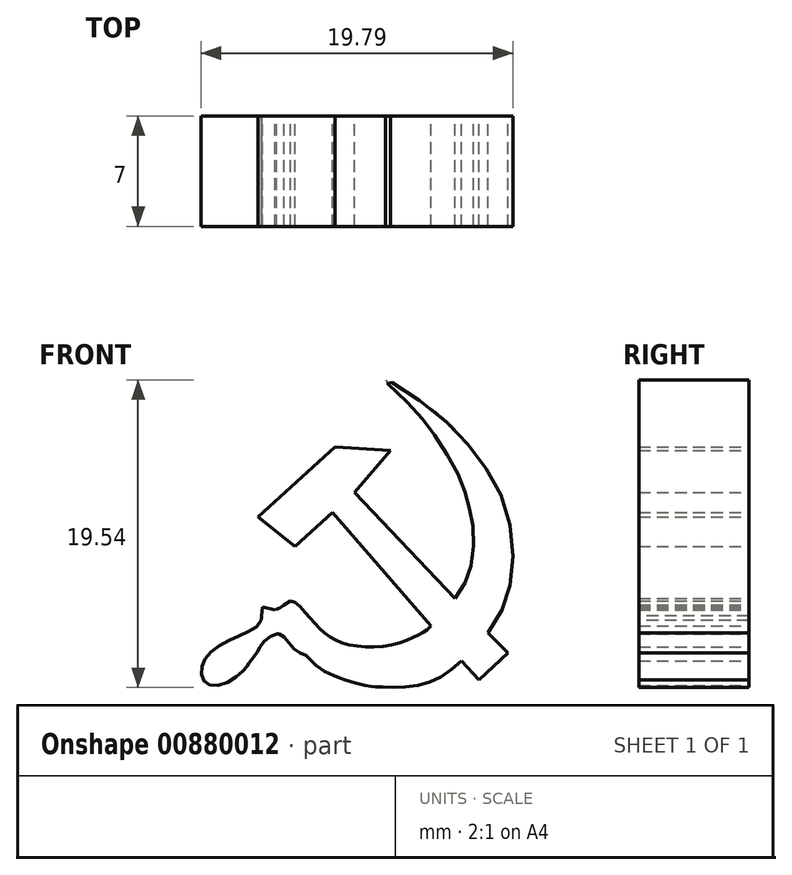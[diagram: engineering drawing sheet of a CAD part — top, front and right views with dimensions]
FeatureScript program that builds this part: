
annotation { "Feature Type Name" : "Feature", "Feature Type Description" : "" }
export const myFeature = defineFeature(function(context is Context, id is Id, definition is map)
    precondition{}
    {
        {
            var Q0;
            Q0=qCreatedBy(makeId("Front.planeOp"),FACE);
            var sketch = newSketch(context, id + "F0", { "sketchPlane" : qUnion([Q0])});
            skLineSegment(sketch, "E0", {"start": v(-4.12, 3.33) * mm, "end": v(-6.5, 1.17) * mm});
            skLineSegment(sketch, "E1", {"start": v(-6.5, 1.17) * mm, "end": v(-8.85, 3.04) * mm});
            skLineSegment(sketch, "E2", {"start": v(-8.85, 3.04) * mm, "end": v(-3.96, 7.5) * mm});
            skLineSegment(sketch, "E3", {"start": v(-3.96, 7.5) * mm, "end": v(-0.42, 7.27) * mm});
            skLineSegment(sketch, "E4", {"start": v(-0.42, 7.27) * mm, "end": v(-2.72, 4.6) * mm});
            skLineSegment(sketch, "E5", {"start": v(-2.72, 4.6) * mm, "end": v(3.66, -2.14) * mm});
            skLineSegment(sketch, "E6", {"start": v(-4.12, 3.33) * mm, "end": v(2.14, -3.89) * mm});
            skLineSegment(sketch, "E7", {"start": v(4.08, -6.1) * mm, "end": v(5.2, -7.29) * mm});
            skLineSegment(sketch, "E8", {"start": v(5.2, -7.29) * mm, "end": v(7.02, -5.6) * mm});
            skLineSegment(sketch, "E9", {"start": v(7.02, -5.6) * mm, "end": v(3.66, -2.14) * mm});
            skLineSegment(sketch, "E10", {"start": v(2.14, -3.89) * mm, "end": v(4.08, -6.1) * mm});
            skLineSegment(sketch, "E11", {"start": v(-6.78, -2.3) * mm, "end": v(-7.77, -2.87) * mm});
            skLineSegment(sketch, "E12", {"start": v(-7.77, -2.87) * mm, "end": v(-8.54, -2.68) * mm});
            skLineSegment(sketch, "E13", {"start": v(-8.54, -2.68) * mm, "end": v(-8.65, -3.54) * mm});
            skLineSegment(sketch, "E14", {"start": v(-7.96, -4.4) * mm, "end": v(-7.3, -4.4) * mm});
            skFitSpline(sketch, "E15", {"points": [v(-0.76, 11.75) * mm, v(0.78, 10.2) * mm, v(2.04, 8.7) * mm, v(3.28, 6.83) * mm, v(4.16, 5.07) * mm, v(4.57, 3.68) * mm, v(4.8, 2.47) * mm, v(4.81, 0.67) * mm, v(4.44, -0.87) * mm, v(3.66, -2.14) * mm, v(2.14, -3.89) * mm, v(1.4, -4.42) * mm, v(-0.28, -5.07) * mm, v(-2.9, -5.1) * mm, v(-4.45, -4.45) * mm, v(-5.68, -3.22) * mm, v(-6.78, -2.3) * mm, v(-7.66, -2.8) * mm, v(-8.54, -2.68) * mm, v(-8.65, -3.54) * mm, v(-9.81, -4.4) * mm, v(-11.75, -5.47) * mm, v(-12.44, -6.64) * mm, v(-12.13, -7.53) * mm, v(-10.79, -7.45) * mm, v(-9.58, -6.5) * mm, v(-9.41, -6.23) * mm, v(-8.95, -5.61) * mm, v(-8.54, -4.96) * mm, v(-7.63, -4.4) * mm, v(-7.1, -4.67) * mm, v(-6.43, -5.46) * mm, v(-5.75, -5.77) * mm, v(-5.2, -6.36) * mm, v(-3.88, -7.1) * mm, v(-3.37, -7.3) * mm, v(-1.84, -7.7) * mm, v(-1.52, -7.73) * mm, v(-0.56, -7.78) * mm, v(1.87, -7.52) * mm, v(4.08, -6.1) * mm, v(6.3, -3.54) * mm, v(7.27, -0.7) * mm, v(6.94, 3.45) * mm, v(5.01, 7.02) * mm, v(1.9, 10.07) * mm, v(-0.76, 11.75) * mm]});
            skSolve(sketch);
        }
        {
            var Q0;
            Q0=makeQuery(id+"F0.imprint","IMPRINT",FACE,{"disambiguationData":[TD([[makeQuery(id+"F0.imprint","IMPRINT",EDGE,{"derivedFrom":sQuery(id+"F0.wireOp",EDGE,"E0")}),-1.0]])]});
            var Q1;
            {var subQ4=sQuery(id+"F0.wireOp",EDGE,"E10");Q1=makeQuery(id+"F0.imprint","IMPRINT",FACE,{"disambiguationData":[TD([[makeQuery(id+"F0.imprint","IMPRINT",EDGE,{"derivedFrom":subQ4}),1.0]])]});}
            var Q2;
            {var subQ0=sQuery(id+"F0.wireOp",EDGE,"E15");var subQ1=sQuery(id+"F0.wireOp",EDGE,"E9");var subQ3=makeQuery(id+"F0.imprint","INTERSECT",VERTEX,{"derivedFrom":[subQ1,subQ0]});Q2=makeQuery(id+"F0.imprint","IMPRINT",FACE,{"disambiguationData":[TD([[makeQuery(id+"F0.imprint","IMPRINT",EDGE,{"disambiguationData":[TD([[subQ3,-1.0]])],"derivedFrom":subQ1}),-1.0]])]});}
            var Q3;
            {var subQ0=sQuery(id+"F0.wireOp",EDGE,"E7");Q3=makeQuery(id+"F0.imprint","IMPRINT",FACE,{"disambiguationData":[TD([[makeQuery(id+"F0.imprint","IMPRINT",EDGE,{"derivedFrom":subQ0}),1.0]])]});}
            var Q4;
            {var subQ1=sQuery(id+"F0.wireOp",EDGE,"E10");Q4=makeQuery(id+"F0.imprint","IMPRINT",FACE,{"disambiguationData":[TD([[makeQuery(id+"F0.imprint","IMPRINT",EDGE,{"derivedFrom":subQ1}),-1.0]])]});}
            extrude(context, id + "F1", {"entities" : qUnion([Q0, Q1, Q2, Q3, Q4]), "depth" : 7 * mm, "offsetDistance" : 25.4 * mm});
        }
    });
